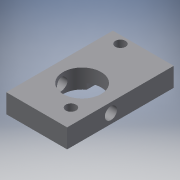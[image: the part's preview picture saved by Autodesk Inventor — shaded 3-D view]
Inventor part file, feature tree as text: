
AUTODESK INVENTOR PART (.ipt)
format: ipt  version: 2016 (Build 200138000, 138)  size: 175,616 bytes
history: native  units: mm
features: extrude x7, sketch x6, projected_geometry x4
ambient origin geometry x8: Origin, YZ Plane, XZ Plane, XY Plane, X Axis, Y Axis, Z Axis, Center Point
bodies: Solid1 (feature_tree)
feature tree (17):
  extrude  "Extrusion1"  Depth=28.0mm
  extrude  "Extrusion3"  Depth=5.0mm
  extrude  "Extrusion4"  Depth=1.5mm TaperAngle=0.0deg
  extrude  "Extrusion5"  Depth=10.0mm
  extrude  "Extrusion6"  Depth=1.5mm
  extrude  "Extrusion8"  Depth=10.0mm
  extrude  "Extrusion9"  Depth=1.5mm TaperAngle=0.0deg
  sketch  "Sketch4"  dims[d0=17.0mm d1=28.0mm]
  projected_geometry  "Projected Loop2"
  sketch  "Sketch5"  dims[d5=5.0mm d6=0.0mm d15=6.0mm]
  projected_geometry  "Projected Loop3"
  sketch  "Sketch6"  dims[d17=5.5mm d18=1.5mm d19=0.0mm]
  projected_geometry  "Projected Loop4"
  sketch  "Sketch7"  dims[d20=10.0mm d21=12.047087mm]
  sketch  "Sketch8"  dims[d22=1.5mm d23=0.0mm d24=2.7mm]
  sketch  "Sketch9"  dims[d25=4.5mm d26=2.0mm d27=1.5mm d28=0.0mm d30=20.0mm d31=4.0mm d32=2.7mm d33=4.5mm d34=5.0mm d35=1.5mm d36=0.0mm d37=3.2mm d41=11.5mm d42=10.0mm d43=0.0mm d44=10.0mm d45=0.0mm d47=0.5mm d48=0.5mm d49=2.5mm]
  projected_geometry  "Projected Loop6"
